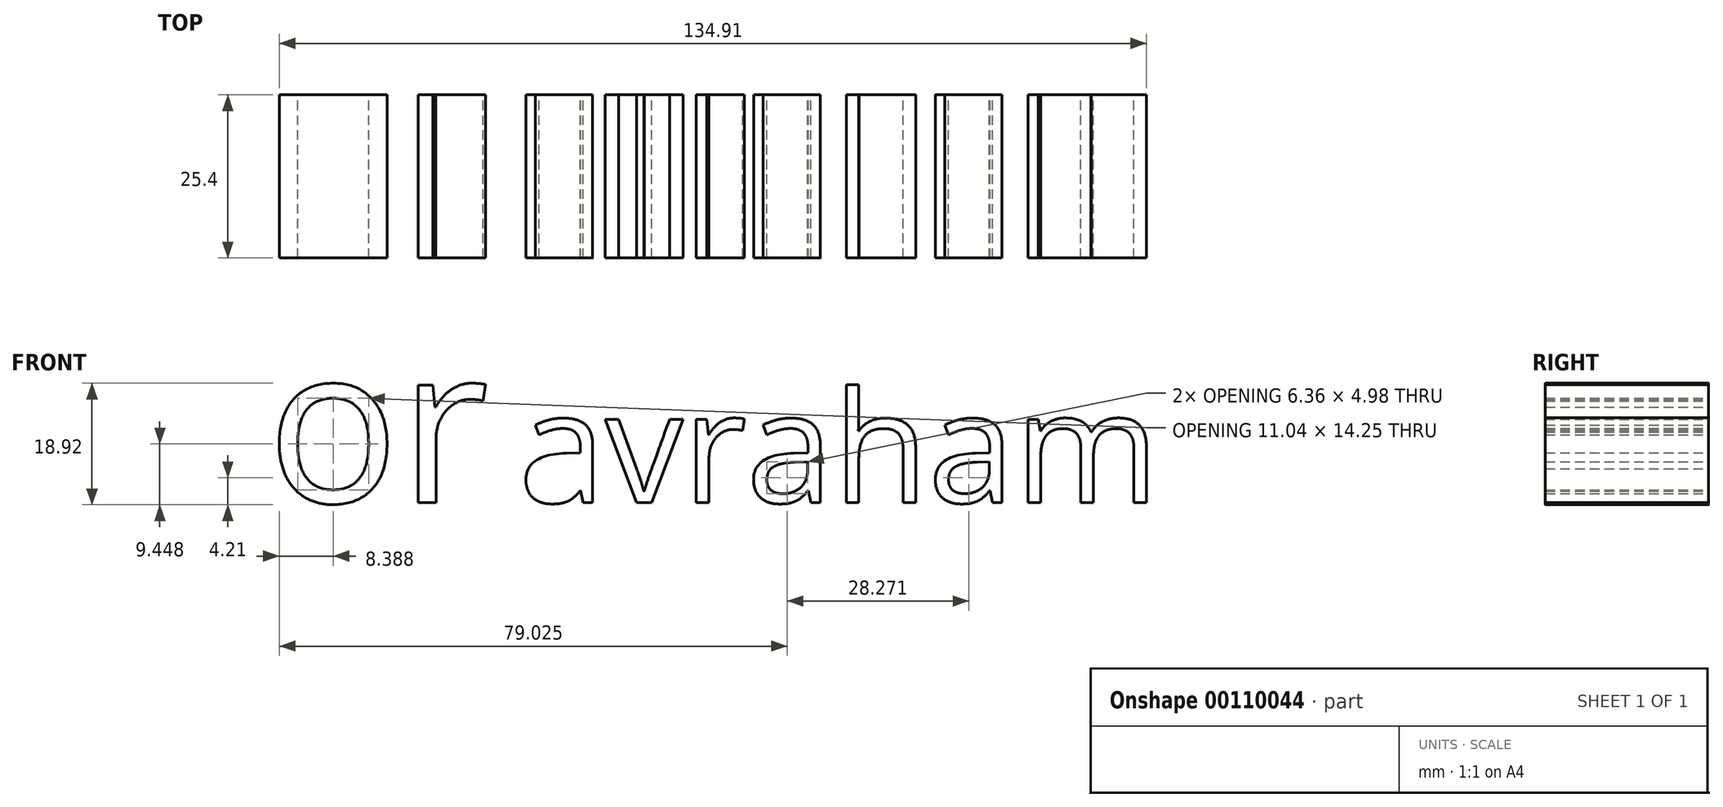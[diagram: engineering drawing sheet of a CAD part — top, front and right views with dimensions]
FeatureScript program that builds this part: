
annotation { "Feature Type Name" : "Feature", "Feature Type Description" : "" }
export const myFeature = defineFeature(function(context is Context, id is Id, definition is map)
    precondition{}
    {
        {
            var Q0;
            Q0=qCreatedBy(makeId("Front.planeOp"),FACE);
            var sketch = newSketch(context, id + "F0", { "sketchPlane" : qUnion([Q0])});
            skText(sketch, "E0", { "text": "or", "fontName": "OpenSans-Regular.ttf"});
            const initialGuessF0  = {"E0": [-0.1538, 0.0316, 1, 0, 0.02455]};
            skSetInitialGuess(sketch, initialGuessF0);
            skSolve(sketch);
        }
        {
            var Q0;
            Q0=makeQuery(id+"F0.imprint","IMPRINT",FACE,{"disambiguationData":[TD([[makeQuery(id+"F0.imprint","IMPRINT",EDGE,{"derivedFrom":sQuery(id+"F0.wireOp",EDGE,"E0.sketch_text.stroke-0")}),-1.0]])]});
            var Q1;
            Q1=makeQuery(id+"F0.imprint","IMPRINT",FACE,{"disambiguationData":[TD([[makeQuery(id+"F0.imprint","IMPRINT",EDGE,{"derivedFrom":sQuery(id+"F0.wireOp",EDGE,"E0.sketch_text.stroke-17")}),-1.0]])]});
            extrude(context, id + "F1", {"entities" : qUnion([Q0, Q1]), "depth" : 25.4 * mm});
        }
        {
            var Q0;
            Q0=qCreatedBy(makeId("Front.planeOp"),FACE);
            var sketch = newSketch(context, id + "F2", { "sketchPlane" : qUnion([Q0])});
            skText(sketch, "E1", { "text": "avraham", "fontName": "OpenSans-Regular.ttf"});
            const initialGuessF2  = {"E1": [-0.11462, 0.0316, 1, 0, 0.0174]};
            skSetInitialGuess(sketch, initialGuessF2);
            skSolve(sketch);
        }
        {
            var Q0;
            Q0=makeQuery(id+"F2.imprint","IMPRINT",FACE,{"disambiguationData":[TD([[makeQuery(id+"F2.imprint","IMPRINT",EDGE,{"derivedFrom":sQuery(id+"F2.wireOp",EDGE,"E1.sketch_text.stroke-27")}),-1.0]])]});
            var Q1;
            Q1=makeQuery(id+"F2.imprint","IMPRINT",FACE,{"disambiguationData":[TD([[makeQuery(id+"F2.imprint","IMPRINT",EDGE,{"derivedFrom":sQuery(id+"F2.wireOp",EDGE,"E1.sketch_text.stroke-37")}),-1.0]])]});
            var Q2;
            Q2=makeQuery(id+"F2.imprint","IMPRINT",FACE,{"disambiguationData":[TD([[makeQuery(id+"F2.imprint","IMPRINT",EDGE,{"derivedFrom":sQuery(id+"F2.wireOp",EDGE,"E1.sketch_text.stroke-77")}),-1.0]])]});
            var Q3;
            Q3=makeQuery(id+"F2.imprint","IMPRINT",FACE,{"disambiguationData":[TD([[makeQuery(id+"F2.imprint","IMPRINT",EDGE,{"derivedFrom":sQuery(id+"F2.wireOp",EDGE,"E1.sketch_text.stroke-122")}),-1.0]])]});
            var Q4;
            Q4=makeQuery(id+"F2.imprint","IMPRINT",FACE,{"disambiguationData":[TD([[makeQuery(id+"F2.imprint","IMPRINT",EDGE,{"derivedFrom":sQuery(id+"F2.wireOp",EDGE,"E1.sketch_text.stroke-0")}),-1.0]])]});
            var Q5;
            Q5=makeQuery(id+"F2.imprint","IMPRINT",FACE,{"disambiguationData":[TD([[makeQuery(id+"F2.imprint","IMPRINT",EDGE,{"derivedFrom":sQuery(id+"F2.wireOp",EDGE,"E1.sketch_text.stroke-50")}),-1.0]])]});
            var Q6;
            Q6=makeQuery(id+"F2.imprint","IMPRINT",FACE,{"disambiguationData":[TD([[makeQuery(id+"F2.imprint","IMPRINT",EDGE,{"derivedFrom":sQuery(id+"F2.wireOp",EDGE,"E1.sketch_text.stroke-95")}),-1.0]])]});
            var Q7;
            Q7 = qSketchRegion(id + "F2", true);
            var Q8;
            Q8=makeQuery(id+"F2.imprint","IMPRINT",FACE,{"disambiguationData":[TD([[makeQuery(id+"F2.imprint","IMPRINT",EDGE,{"derivedFrom":sQuery(id+"F2.wireOp",EDGE,"E1.sketch_text.stroke-19")}),1.0]])]});
            extrude(context, id + "F3", {"entities" : qUnion([Q0, Q1, Q2, Q3, Q4, Q5, Q6, Q7, Q8]), "depth" : 25.4 * mm});
        }
    });
